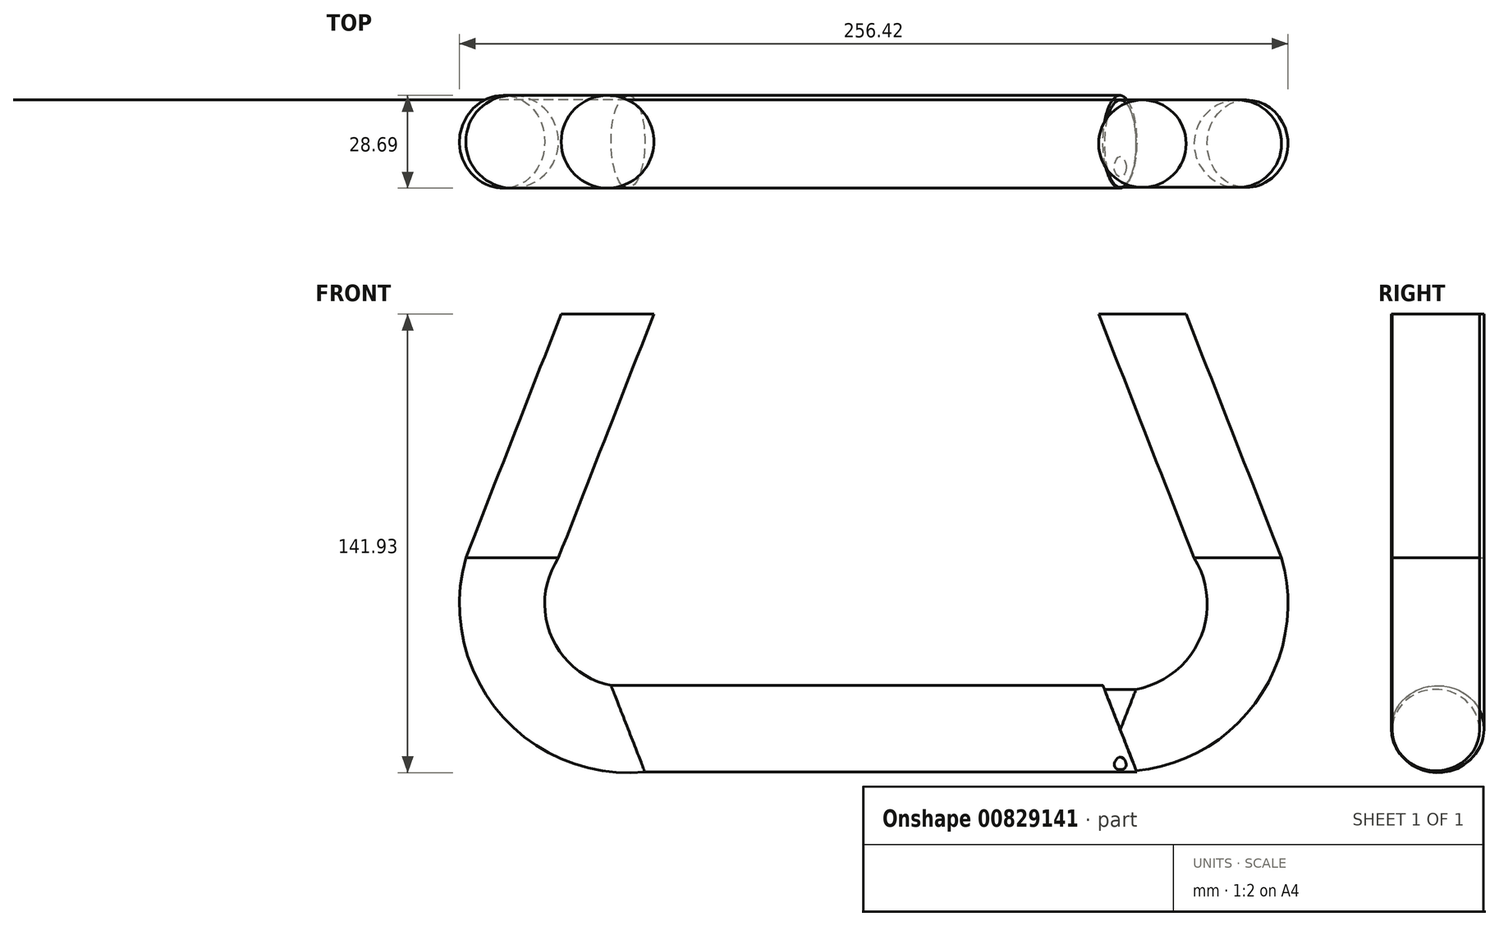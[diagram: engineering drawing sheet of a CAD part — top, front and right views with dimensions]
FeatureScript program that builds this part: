
annotation { "Feature Type Name" : "Feature", "Feature Type Description" : "" }
export const myFeature = defineFeature(function(context is Context, id is Id, definition is map)
    precondition{}
    {
        {
            var Q0;
            Q0=qCreatedBy(makeId("Front.planeOp"),FACE);
            var sketch = newSketch(context, id + "F0", { "sketchPlane" : qUnion([Q0])});
            skLineSegment(sketch, "E0", {"start": v(76.82, -77.82) * mm, "end": v(-75.42, -77.82) * mm});
            skArc(sketch, "E1", {"start": v(-111.7, -24.65) * mm, "mid": v(-107.6, -60.81) * mm, "end": v(-75.42, -77.82) * mm});
            skArc(sketch, "E2", {"start": v(76.82, -77.82) * mm, "mid": v(109, -60.81) * mm, "end": v(113.1, -24.65) * mm});
            skLineSegment(sketch, "E3", {"start": v(-82.18, 50.8) * mm, "end": v(-111.7, -24.65) * mm});
            skLineSegment(sketch, "E4", {"start": v(83.57, 50.8) * mm, "end": v(113.1, -24.65) * mm});
            skPoint(sketch, "E5.start.orphan", {"position": v(0.7, -77.82) * mm});
            skLineSegment(sketch, "E6", {"start": v(0.7, -77.82) * mm, "end": v(0.7, 55.43) * mm, "construction": true});
            skLineSegment(sketch, "E7", {"start": v(0.7, 55.43) * mm, "end": v(-146.75, 55.43) * mm, "construction": true});
            skLineSegment(sketch, "E8", {"start": v(0.7, 55.43) * mm, "end": v(163.93, 55.43) * mm, "construction": true});
            skLineSegment(sketch, "E9.0", {"start": v(69.93, 50.8) * mm, "end": v(101.28, -29.27) * mm});
            skArc(sketch, "E10.0", {"start": v(76.82, -90.52) * mm, "mid": v(119.5, -67.97) * mm, "end": v(124.93, -20.02) * mm});
            skArc(sketch, "E11.0", {"start": v(76.82, -65.12) * mm, "mid": v(98.51, -53.66) * mm, "end": v(101.28, -29.27) * mm});
            skLineSegment(sketch, "E12.0", {"start": v(76.82, -65.12) * mm, "end": v(-75.42, -65.12) * mm});
            skLineSegment(sketch, "E13.0", {"start": v(76.82, -90.52) * mm, "end": v(-75.42, -90.52) * mm});
            skArc(sketch, "E14.0", {"start": v(-123.53, -20.02) * mm, "mid": v(-118.1, -67.97) * mm, "end": v(-75.42, -90.52) * mm});
            skArc(sketch, "E15.0", {"start": v(-99.88, -29.27) * mm, "mid": v(-97.11, -53.66) * mm, "end": v(-75.42, -65.12) * mm});
            skLineSegment(sketch, "E16.0", {"start": v(-68.54, 50.8) * mm, "end": v(-99.88, -29.27) * mm});
            skLineSegment(sketch, "E17", {"start": v(69.93, 50.8) * mm, "end": v(97.21, 50.8) * mm});
            skLineSegment(sketch, "E18", {"start": v(-68.54, 50.8) * mm, "end": v(-95.81, 50.8) * mm});
            skLineSegment(sketch, "E19.trimOffspring", {"start": v(97.21, 50.8) * mm, "end": v(124.93, -20.02) * mm});
            skLineSegment(sketch, "E20.trimOffspring", {"start": v(-95.81, 50.8) * mm, "end": v(-123.53, -20.02) * mm});
            skSolve(sketch);
        }
        {
            var Q0;
            Q0=sQuery(id+"F0.wireOp",VERTEX,"E0.start");
            var Q1;
            Q1=sQuery(id+"F0.wireOp",EDGE,"E0");
            cPlane(context, id + "F1", {"entities" : qUnion([Q0, Q1]), "cplaneType" : CPlaneType.LINE_POINT, "offset" : 25.4 * mm, "width" : 152.4 * mm, "height" : 152.4 * mm});
        }
        {
            var Q0;
            Q0=sQuery(id+"F0.wireOp",EDGE,"E17");
            cPlane(context, id + "F2", {"entities" : qUnion([Q0]), "cplaneType" : CPlaneType.LINE_ANGLE, "offset" : 25.4 * mm, "angle" : 90 * degree, "width" : 152.4 * mm, "height" : 152.4 * mm});
        }
        {
            var Q0;
            Q0=qCreatedBy(id+"F2.planeOp",FACE);
            var sketch = newSketch(context, id + "F3", { "sketchPlane" : qUnion([Q0])});
            skCircle(sketch, "E21", {"center": v(83.68, -1.2) * mm, "radius": 13.53 * mm});
            skPoint(sketch, "E21.first.point", {"position": v(70.2, 0) * mm});
            skPoint(sketch, "E21.second.point", {"position": v(97.15, 0) * mm});
            skPoint(sketch, "E21.third.point", {"position": v(83.32, -14.72) * mm});
            skSolve(sketch);
        }
        {
            var Q0;
            Q0=makeQuery(id+"F3.imprint","IMPRINT",FACE,{"disambiguationData":[TD([[makeQuery(id+"F3.imprint","IMPRINT",EDGE,{"derivedFrom":sQuery(id+"F3.wireOp",EDGE,"E21")}),1.0]])]});
            var Q1;
            Q1=sQuery(id+"F0.wireOp",EDGE,"E4");
            var Q2;
            Q2=sQuery(id+"F0.wireOp",EDGE,"E2");
            var Q3;
            Q3=sQuery(id+"F0.wireOp",EDGE,"E0");
            sweep(context, id + "F4", {"profiles" : qUnion([Q0]), "path" : qUnion([Q1, Q2, Q3])});
        }
        {
            var Q0;
            Q0=sQuery(id+"F0.wireOp",EDGE,"E18");
            cPlane(context, id + "F5", {"entities" : qUnion([Q0]), "cplaneType" : CPlaneType.LINE_ANGLE, "offset" : 25.4 * mm, "angle" : 90 * degree, "width" : 152.4 * mm, "height" : 152.4 * mm});
        }
        {
            var Q0;
            Q0=qCreatedBy(id+"F5.planeOp",FACE);
            var sketch = newSketch(context, id + "F6", { "sketchPlane" : qUnion([Q0])});
            skCircle(sketch, "E22", {"center": v(-81.86, -0.6) * mm, "radius": 14.34 * mm});
            skPoint(sketch, "E22.first.point", {"position": v(-96.19, 0) * mm});
            skPoint(sketch, "E22.second.point", {"position": v(-67.53, 0) * mm});
            skPoint(sketch, "E22.third.point", {"position": v(-78.63, 13.38) * mm});
            skSolve(sketch);
        }
        {
            var Q0;
            Q0=makeQuery(id+"F6.imprint","IMPRINT",FACE,{"disambiguationData":[TD([[makeQuery(id+"F6.imprint","IMPRINT",EDGE,{"derivedFrom":sQuery(id+"F6.wireOp",EDGE,"E22")}),1.0]])]});
            var Q1;
            Q1=sQuery(id+"F0.wireOp",EDGE,"E3");
            var Q2;
            Q2=sQuery(id+"F0.wireOp",EDGE,"E1");
            var Q3;
            Q3=sQuery(id+"F0.wireOp",EDGE,"E0");
            sweep(context, id + "F7", {"operationType" : NewBodyOperationType.ADD, "profiles" : qUnion([Q0]), "path" : qUnion([Q1, Q2, Q3])});
        }
    });
